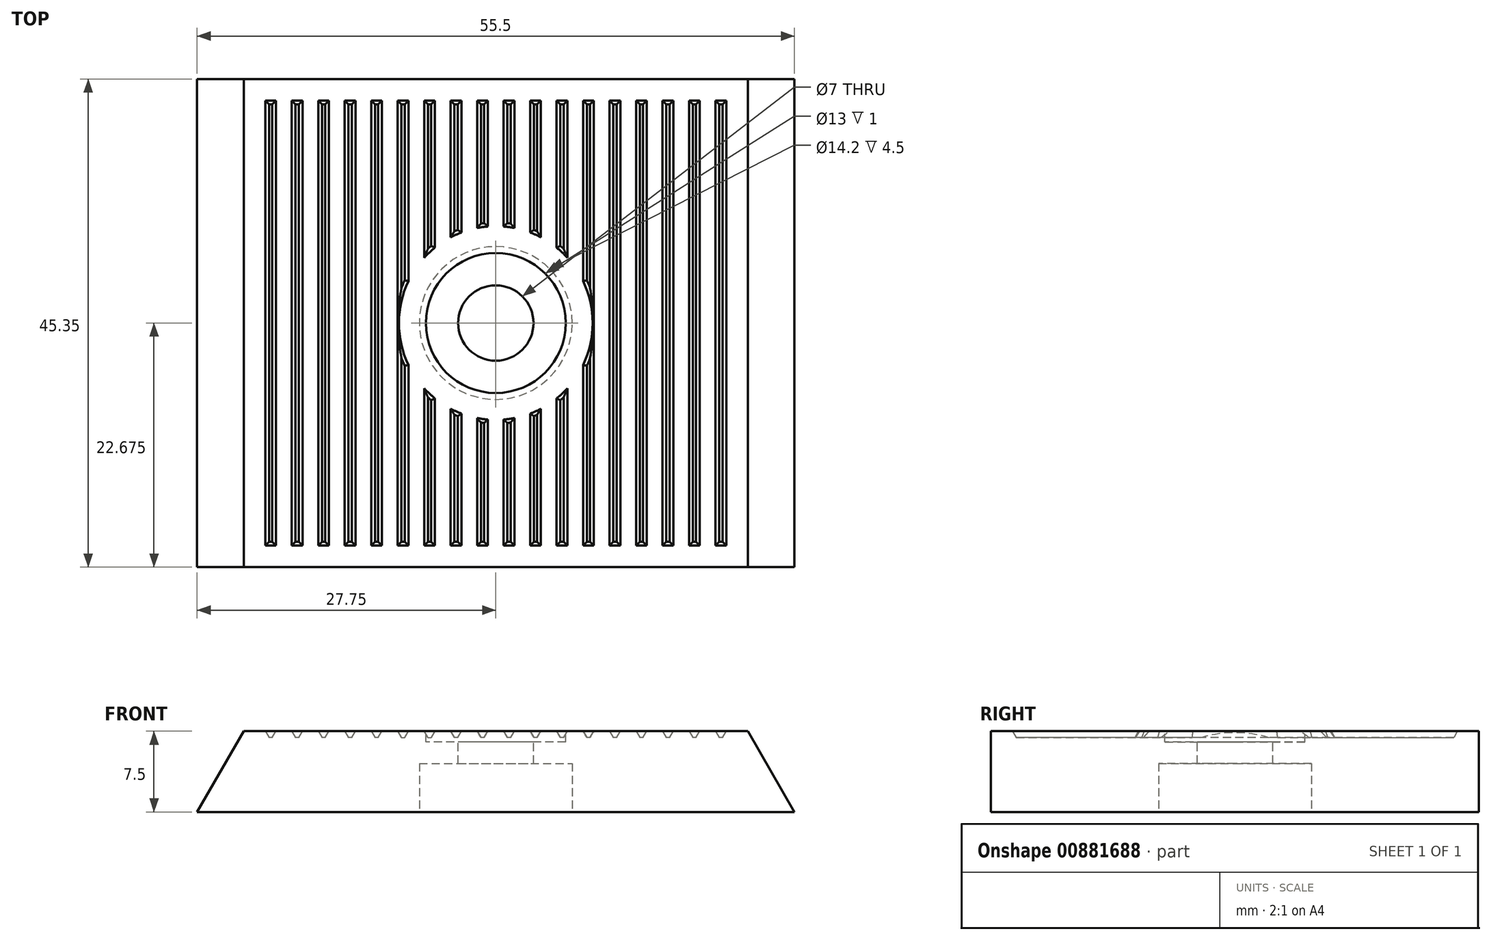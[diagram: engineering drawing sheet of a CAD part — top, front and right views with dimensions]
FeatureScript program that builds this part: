
annotation { "Feature Type Name" : "Feature", "Feature Type Description" : "" }
export const myFeature = defineFeature(function(context is Context, id is Id, definition is map)
    precondition{}
    {
        {
            var Q0;
            Q0=qCreatedBy(makeId("Front.planeOp"),FACE);
            var sketch = newSketch(context, id + "F0", { "sketchPlane" : qUnion([Q0])});
            skLineSegment(sketch, "E0", {"start": v(0, 0) * mm, "end": v(-55.5, 0) * mm});
            skLineSegment(sketch, "E1", {"start": v(-55.5, 0) * mm, "end": v(-51.17, 7.5) * mm});
            skLineSegment(sketch, "E2", {"start": v(-51.17, 7.5) * mm, "end": v(-4.33, 7.5) * mm});
            skLineSegment(sketch, "E3", {"start": v(-4.33, 7.5) * mm, "end": v(0, 0) * mm});
            skSolve(sketch);
        }
        {
            var Q0;
            Q0=makeQuery(id+"F0.imprint","IMPRINT",FACE,{"disambiguationData":[TD([[makeQuery(id+"F0.imprint","IMPRINT",EDGE,{"derivedFrom":sQuery(id+"F0.wireOp",EDGE,"E0")}),-1.0]])]});
            extrude(context, id + "F1", {"entities" : qUnion([Q0]), "depth" : 45.35 * mm, "offsetDistance" : 25 * mm});
        }
        {
            var Q0;
            Q0=makeQuery(id+"F1.opExtrude","SWEPT_FACE",FACE,{"disambiguationData":[OSD([sQuery(id+"F0.wireOp",EDGE,"E2")])]});
            var sketch = newSketch(context, id + "F2", { "sketchPlane" : qUnion([Q0])});
            skLineSegment(sketch, "E4.bottom", {"start": v(-49.17, -2) * mm, "end": v(-48.17, -2) * mm});
            skLineSegment(sketch, "E4.top", {"start": v(-49.17, -43.35) * mm, "end": v(-48.17, -43.35) * mm});
            skLineSegment(sketch, "E4.left", {"start": v(-49.17, -2) * mm, "end": v(-49.17, -43.35) * mm});
            skLineSegment(sketch, "E4.right", {"start": v(-48.17, -2) * mm, "end": v(-48.17, -43.35) * mm});
            skLineSegment(sketch, "E5.1.0.0", {"start": v(-46.7, -2) * mm, "end": v(-46.7, -43.35) * mm});
            skLineSegment(sketch, "E5.1.0.1", {"start": v(-45.7, -2) * mm, "end": v(-45.7, -43.35) * mm});
            skLineSegment(sketch, "E5.1.0.2", {"start": v(-46.7, -2) * mm, "end": v(-45.7, -2) * mm});
            skLineSegment(sketch, "E5.1.0.3", {"start": v(-46.7, -43.35) * mm, "end": v(-45.7, -43.35) * mm});
            skLineSegment(sketch, "E5.2.0.0", {"start": v(-44.25, -2) * mm, "end": v(-44.25, -43.35) * mm});
            skLineSegment(sketch, "E5.2.0.1", {"start": v(-43.25, -2) * mm, "end": v(-43.25, -43.35) * mm});
            skLineSegment(sketch, "E5.2.0.2", {"start": v(-44.25, -2) * mm, "end": v(-43.25, -2) * mm});
            skLineSegment(sketch, "E5.2.0.3", {"start": v(-44.25, -43.35) * mm, "end": v(-43.25, -43.35) * mm});
            skLineSegment(sketch, "E5.direction1", {"start": v(-49.17, -43.35) * mm, "end": v(-46.7, -43.35) * mm, "construction": true});
            skLineSegment(sketch, "E6.0.3.0", {"start": v(-41.79, -2) * mm, "end": v(-41.79, -43.35) * mm});
            skLineSegment(sketch, "E6.3.3.0", {"start": v(-40.79, -2) * mm, "end": v(-40.79, -43.35) * mm});
            skLineSegment(sketch, "E6.6.3.0", {"start": v(-41.79, -2) * mm, "end": v(-40.79, -2) * mm});
            skLineSegment(sketch, "E6.9.3.0", {"start": v(-41.79, -43.35) * mm, "end": v(-40.79, -43.35) * mm});
            skLineSegment(sketch, "E6.0.4.0", {"start": v(-39.33, -2) * mm, "end": v(-39.33, -43.35) * mm});
            skLineSegment(sketch, "E6.3.4.0", {"start": v(-38.33, -2) * mm, "end": v(-38.33, -43.35) * mm});
            skLineSegment(sketch, "E6.6.4.0", {"start": v(-39.33, -2) * mm, "end": v(-38.33, -2) * mm});
            skLineSegment(sketch, "E6.9.4.0", {"start": v(-39.33, -43.35) * mm, "end": v(-38.33, -43.35) * mm});
            skLineSegment(sketch, "E6.0.5.0", {"start": v(-36.86, -2) * mm, "end": v(-36.86, -43.35) * mm});
            skLineSegment(sketch, "E6.3.5.0", {"start": v(-35.86, -2) * mm, "end": v(-35.86, -18.78) * mm});
            skLineSegment(sketch, "E6.6.5.0", {"start": v(-36.86, -2) * mm, "end": v(-35.86, -2) * mm});
            skLineSegment(sketch, "E6.9.5.0", {"start": v(-36.86, -43.35) * mm, "end": v(-35.86, -43.35) * mm});
            skLineSegment(sketch, "E6.0.6.0", {"start": v(-34.4, -2) * mm, "end": v(-34.4, -16.61) * mm});
            skLineSegment(sketch, "E6.3.6.0", {"start": v(-33.4, -2) * mm, "end": v(-33.4, -15.67) * mm});
            skLineSegment(sketch, "E6.6.6.0", {"start": v(-34.4, -2) * mm, "end": v(-33.4, -2) * mm});
            skLineSegment(sketch, "E6.9.6.0", {"start": v(-34.4, -43.35) * mm, "end": v(-33.4, -43.35) * mm});
            skLineSegment(sketch, "E6.0.7.0", {"start": v(-31.94, -2) * mm, "end": v(-31.94, -14.71) * mm});
            skLineSegment(sketch, "E6.3.7.0", {"start": v(-30.94, -2) * mm, "end": v(-30.94, -14.26) * mm});
            skLineSegment(sketch, "E6.6.7.0", {"start": v(-31.94, -2) * mm, "end": v(-30.94, -2) * mm});
            skLineSegment(sketch, "E6.9.7.0", {"start": v(-31.94, -43.35) * mm, "end": v(-30.94, -43.35) * mm});
            skLineSegment(sketch, "E6.0.8.0", {"start": v(-29.48, -2) * mm, "end": v(-29.48, -13.84) * mm});
            skLineSegment(sketch, "E6.3.8.0", {"start": v(-28.48, -2) * mm, "end": v(-28.48, -13.7) * mm});
            skLineSegment(sketch, "E6.6.8.0", {"start": v(-29.48, -2) * mm, "end": v(-28.48, -2) * mm});
            skLineSegment(sketch, "E6.9.8.0", {"start": v(-29.48, -43.35) * mm, "end": v(-28.48, -43.35) * mm});
            skLineSegment(sketch, "E6.0.9.0", {"start": v(-27.02, -2) * mm, "end": v(-27.02, -13.7) * mm});
            skLineSegment(sketch, "E6.3.9.0", {"start": v(-26.02, -2) * mm, "end": v(-26.02, -13.84) * mm});
            skLineSegment(sketch, "E6.6.9.0", {"start": v(-27.02, -2) * mm, "end": v(-26.02, -2) * mm});
            skLineSegment(sketch, "E6.9.9.0", {"start": v(-27.02, -43.35) * mm, "end": v(-26.02, -43.35) * mm});
            skLineSegment(sketch, "E6.0.10.0", {"start": v(-24.56, -2) * mm, "end": v(-24.56, -14.26) * mm});
            skLineSegment(sketch, "E6.3.10.0", {"start": v(-23.56, -2) * mm, "end": v(-23.56, -14.71) * mm});
            skLineSegment(sketch, "E6.6.10.0", {"start": v(-24.56, -2) * mm, "end": v(-23.56, -2) * mm});
            skLineSegment(sketch, "E6.9.10.0", {"start": v(-24.56, -43.35) * mm, "end": v(-23.56, -43.35) * mm});
            skLineSegment(sketch, "E6.0.11.0", {"start": v(-22.1, -2) * mm, "end": v(-22.1, -15.67) * mm});
            skLineSegment(sketch, "E6.3.11.0", {"start": v(-21.1, -2) * mm, "end": v(-21.1, -16.61) * mm});
            skLineSegment(sketch, "E6.6.11.0", {"start": v(-22.1, -2) * mm, "end": v(-21.1, -2) * mm});
            skLineSegment(sketch, "E6.9.11.0", {"start": v(-22.1, -43.35) * mm, "end": v(-21.1, -43.35) * mm});
            skLineSegment(sketch, "E6.0.12.0", {"start": v(-19.64, -2) * mm, "end": v(-19.64, -18.78) * mm});
            skLineSegment(sketch, "E6.3.12.0", {"start": v(-18.64, -2) * mm, "end": v(-18.64, -43.35) * mm});
            skLineSegment(sketch, "E6.6.12.0", {"start": v(-19.64, -2) * mm, "end": v(-18.64, -2) * mm});
            skLineSegment(sketch, "E6.9.12.0", {"start": v(-19.64, -43.35) * mm, "end": v(-18.64, -43.35) * mm});
            skLineSegment(sketch, "E6.0.13.0", {"start": v(-17.17, -2) * mm, "end": v(-17.17, -43.35) * mm});
            skLineSegment(sketch, "E6.3.13.0", {"start": v(-16.17, -2) * mm, "end": v(-16.17, -43.35) * mm});
            skLineSegment(sketch, "E6.6.13.0", {"start": v(-17.17, -2) * mm, "end": v(-16.17, -2) * mm});
            skLineSegment(sketch, "E6.9.13.0", {"start": v(-17.17, -43.35) * mm, "end": v(-16.17, -43.35) * mm});
            skLineSegment(sketch, "E6.0.14.0", {"start": v(-14.71, -2) * mm, "end": v(-14.71, -43.35) * mm});
            skLineSegment(sketch, "E6.3.14.0", {"start": v(-13.71, -2) * mm, "end": v(-13.71, -43.35) * mm});
            skLineSegment(sketch, "E6.6.14.0", {"start": v(-14.71, -2) * mm, "end": v(-13.71, -2) * mm});
            skLineSegment(sketch, "E6.9.14.0", {"start": v(-14.71, -43.35) * mm, "end": v(-13.71, -43.35) * mm});
            skLineSegment(sketch, "E6.0.15.0", {"start": v(-12.25, -2) * mm, "end": v(-12.25, -43.35) * mm});
            skLineSegment(sketch, "E6.3.15.0", {"start": v(-11.25, -2) * mm, "end": v(-11.25, -43.35) * mm});
            skLineSegment(sketch, "E6.6.15.0", {"start": v(-12.25, -2) * mm, "end": v(-11.25, -2) * mm});
            skLineSegment(sketch, "E6.9.15.0", {"start": v(-12.25, -43.35) * mm, "end": v(-11.25, -43.35) * mm});
            skLineSegment(sketch, "E6.0.16.0", {"start": v(-9.8, -2) * mm, "end": v(-9.8, -43.35) * mm});
            skLineSegment(sketch, "E6.3.16.0", {"start": v(-8.8, -2) * mm, "end": v(-8.8, -43.35) * mm});
            skLineSegment(sketch, "E6.6.16.0", {"start": v(-9.8, -2) * mm, "end": v(-8.8, -2) * mm});
            skLineSegment(sketch, "E6.9.16.0", {"start": v(-9.8, -43.35) * mm, "end": v(-8.8, -43.35) * mm});
            skLineSegment(sketch, "E6.0.17.0", {"start": v(-7.33, -2) * mm, "end": v(-7.33, -43.35) * mm});
            skLineSegment(sketch, "E6.3.17.0", {"start": v(-6.33, -2) * mm, "end": v(-6.33, -43.35) * mm});
            skLineSegment(sketch, "E6.6.17.0", {"start": v(-7.33, -2) * mm, "end": v(-6.33, -2) * mm});
            skLineSegment(sketch, "E6.9.17.0", {"start": v(-7.33, -43.35) * mm, "end": v(-6.33, -43.35) * mm});
            skCircle(sketch, "E7.0", {"center": v(-27.75, -22.68) * mm, "radius": 9 * mm});
            skLineSegment(sketch, "E8", {"start": v(-51.17, 0) * mm, "end": v(-4.33, -45.35) * mm, "construction": true});
            skLineSegment(sketch, "E9.trimOffspring", {"start": v(-30.94, -31.1) * mm, "end": v(-30.94, -43.35) * mm});
            skLineSegment(sketch, "E10.trimOffspring", {"start": v(-31.94, -30.64) * mm, "end": v(-31.94, -43.35) * mm});
            skLineSegment(sketch, "E11.trimOffspring", {"start": v(-33.4, -29.68) * mm, "end": v(-33.4, -43.35) * mm});
            skLineSegment(sketch, "E12.trimOffspring", {"start": v(-34.4, -28.74) * mm, "end": v(-34.4, -43.35) * mm});
            skLineSegment(sketch, "E13.trimOffspring", {"start": v(-35.86, -26.57) * mm, "end": v(-35.86, -43.35) * mm});
            skLineSegment(sketch, "E14.trimOffspring", {"start": v(-29.48, -31.5) * mm, "end": v(-29.48, -43.35) * mm});
            skLineSegment(sketch, "E15.trimOffspring", {"start": v(-28.48, -31.65) * mm, "end": v(-28.48, -43.35) * mm});
            skLineSegment(sketch, "E16.trimOffspring", {"start": v(-27.02, -31.65) * mm, "end": v(-27.02, -43.35) * mm});
            skLineSegment(sketch, "E17.trimOffspring", {"start": v(-26.02, -31.5) * mm, "end": v(-26.02, -43.35) * mm});
            skLineSegment(sketch, "E18.trimOffspring", {"start": v(-24.56, -31.1) * mm, "end": v(-24.56, -43.35) * mm});
            skLineSegment(sketch, "E19.trimOffspring", {"start": v(-23.56, -30.64) * mm, "end": v(-23.56, -43.35) * mm});
            skLineSegment(sketch, "E20.trimOffspring", {"start": v(-22.1, -29.68) * mm, "end": v(-22.1, -43.35) * mm});
            skLineSegment(sketch, "E21.trimOffspring", {"start": v(-21.1, -28.74) * mm, "end": v(-21.1, -43.35) * mm});
            skLineSegment(sketch, "E22.trimOffspring", {"start": v(-19.64, -26.57) * mm, "end": v(-19.64, -43.35) * mm});
            skCircle(sketch, "E23", {"center": v(-27.75, -22.68) * mm, "radius": 6.5 * mm});
            skCircle(sketch, "E24", {"center": v(-27.75, -22.68) * mm, "radius": 3.5 * mm});
            skSolve(sketch);
        }
        {
            var Q0;
            Q0=makeQuery(id+"F2.imprint","IMPRINT",FACE,{"disambiguationData":[TD([[makeQuery(id+"F2.imprint","IMPRINT",EDGE,{"derivedFrom":sQuery(id+"F2.wireOp",EDGE,"E4.bottom")}),-1.0]])]});
            var Q1;
            Q1=makeQuery(id+"F2.imprint","IMPRINT",FACE,{"disambiguationData":[TD([[makeQuery(id+"F2.imprint","IMPRINT",EDGE,{"derivedFrom":sQuery(id+"F2.wireOp",EDGE,"E5.1.0.0")}),1.0]])]});
            var Q2;
            Q2=makeQuery(id+"F2.imprint","IMPRINT",FACE,{"disambiguationData":[TD([[makeQuery(id+"F2.imprint","IMPRINT",EDGE,{"derivedFrom":sQuery(id+"F2.wireOp",EDGE,"E5.2.0.0")}),1.0]])]});
            var Q3;
            Q3=makeQuery(id+"F2.imprint","IMPRINT",FACE,{"disambiguationData":[TD([[makeQuery(id+"F2.imprint","IMPRINT",EDGE,{"derivedFrom":sQuery(id+"F2.wireOp",EDGE,"E6.0.3.0")}),1.0]])]});
            var Q4;
            Q4=makeQuery(id+"F2.imprint","IMPRINT",FACE,{"disambiguationData":[TD([[makeQuery(id+"F2.imprint","IMPRINT",EDGE,{"derivedFrom":sQuery(id+"F2.wireOp",EDGE,"E6.0.4.0")}),1.0]])]});
            var Q5;
            Q5=makeQuery(id+"F2.imprint","IMPRINT",FACE,{"disambiguationData":[TD([[makeQuery(id+"F2.imprint","IMPRINT",EDGE,{"derivedFrom":sQuery(id+"F2.wireOp",EDGE,"E6.0.13.0")}),1.0]])]});
            var Q6;
            Q6=makeQuery(id+"F2.imprint","IMPRINT",FACE,{"disambiguationData":[TD([[makeQuery(id+"F2.imprint","IMPRINT",EDGE,{"derivedFrom":sQuery(id+"F2.wireOp",EDGE,"E6.0.14.0")}),1.0]])]});
            var Q7;
            Q7=makeQuery(id+"F2.imprint","IMPRINT",FACE,{"disambiguationData":[TD([[makeQuery(id+"F2.imprint","IMPRINT",EDGE,{"derivedFrom":sQuery(id+"F2.wireOp",EDGE,"E6.0.15.0")}),1.0]])]});
            var Q8;
            Q8=makeQuery(id+"F2.imprint","IMPRINT",FACE,{"disambiguationData":[TD([[makeQuery(id+"F2.imprint","IMPRINT",EDGE,{"derivedFrom":sQuery(id+"F2.wireOp",EDGE,"E6.0.16.0")}),1.0]])]});
            var Q9;
            Q9=makeQuery(id+"F2.imprint","IMPRINT",FACE,{"disambiguationData":[TD([[makeQuery(id+"F2.imprint","IMPRINT",EDGE,{"derivedFrom":sQuery(id+"F2.wireOp",EDGE,"E6.0.17.0")}),1.0]])]});
            var Q10;
            Q10=makeQuery(id+"F2.imprint","IMPRINT",FACE,{"disambiguationData":[TD([[makeQuery(id+"F2.imprint","IMPRINT",EDGE,{"derivedFrom":sQuery(id+"F2.wireOp",EDGE,"E6.0.5.0")}),1.0]])]});
            var Q11;
            {var subQ0=sQuery(id+"F2.wireOp",EDGE,"E6.0.6.0");Q11=makeQuery(id+"F2.imprint","IMPRINT",FACE,{"disambiguationData":[TD([[makeQuery(id+"F2.imprint","IMPRINT",EDGE,{"derivedFrom":subQ0}),1.0]])]});}
            var Q12;
            Q12=makeQuery(id+"F2.imprint","IMPRINT",FACE,{"disambiguationData":[TD([[makeQuery(id+"F2.imprint","IMPRINT",EDGE,{"derivedFrom":sQuery(id+"F2.wireOp",EDGE,"E6.9.6.0")}),1.0]])]});
            var Q13;
            {var subQ0=sQuery(id+"F2.wireOp",EDGE,"E6.0.7.0");Q13=makeQuery(id+"F2.imprint","IMPRINT",FACE,{"disambiguationData":[TD([[makeQuery(id+"F2.imprint","IMPRINT",EDGE,{"derivedFrom":subQ0}),1.0]])]});}
            var Q14;
            Q14=makeQuery(id+"F2.imprint","IMPRINT",FACE,{"disambiguationData":[TD([[makeQuery(id+"F2.imprint","IMPRINT",EDGE,{"derivedFrom":sQuery(id+"F2.wireOp",EDGE,"E6.9.7.0")}),1.0]])]});
            var Q15;
            {var subQ0=sQuery(id+"F2.wireOp",EDGE,"E6.0.8.0");Q15=makeQuery(id+"F2.imprint","IMPRINT",FACE,{"disambiguationData":[TD([[makeQuery(id+"F2.imprint","IMPRINT",EDGE,{"derivedFrom":subQ0}),1.0]])]});}
            var Q16;
            Q16=makeQuery(id+"F2.imprint","IMPRINT",FACE,{"disambiguationData":[TD([[makeQuery(id+"F2.imprint","IMPRINT",EDGE,{"derivedFrom":sQuery(id+"F2.wireOp",EDGE,"E6.9.8.0")}),1.0]])]});
            var Q17;
            {var subQ0=sQuery(id+"F2.wireOp",EDGE,"E6.0.9.0");Q17=makeQuery(id+"F2.imprint","IMPRINT",FACE,{"disambiguationData":[TD([[makeQuery(id+"F2.imprint","IMPRINT",EDGE,{"derivedFrom":subQ0}),1.0]])]});}
            var Q18;
            Q18=makeQuery(id+"F2.imprint","IMPRINT",FACE,{"disambiguationData":[TD([[makeQuery(id+"F2.imprint","IMPRINT",EDGE,{"derivedFrom":sQuery(id+"F2.wireOp",EDGE,"E6.9.9.0")}),1.0]])]});
            var Q19;
            {var subQ0=sQuery(id+"F2.wireOp",EDGE,"E6.0.10.0");Q19=makeQuery(id+"F2.imprint","IMPRINT",FACE,{"disambiguationData":[TD([[makeQuery(id+"F2.imprint","IMPRINT",EDGE,{"derivedFrom":subQ0}),1.0]])]});}
            var Q20;
            Q20=makeQuery(id+"F2.imprint","IMPRINT",FACE,{"disambiguationData":[TD([[makeQuery(id+"F2.imprint","IMPRINT",EDGE,{"derivedFrom":sQuery(id+"F2.wireOp",EDGE,"E6.9.10.0")}),1.0]])]});
            var Q21;
            {var subQ0=sQuery(id+"F2.wireOp",EDGE,"E6.0.11.0");Q21=makeQuery(id+"F2.imprint","IMPRINT",FACE,{"disambiguationData":[TD([[makeQuery(id+"F2.imprint","IMPRINT",EDGE,{"derivedFrom":subQ0}),1.0]])]});}
            var Q22;
            Q22=makeQuery(id+"F2.imprint","IMPRINT",FACE,{"disambiguationData":[TD([[makeQuery(id+"F2.imprint","IMPRINT",EDGE,{"derivedFrom":sQuery(id+"F2.wireOp",EDGE,"E6.9.11.0")}),1.0]])]});
            var Q23;
            {var subQ0=sQuery(id+"F2.wireOp",EDGE,"E6.0.12.0");Q23=makeQuery(id+"F2.imprint","IMPRINT",FACE,{"disambiguationData":[TD([[makeQuery(id+"F2.imprint","IMPRINT",EDGE,{"derivedFrom":subQ0}),1.0]])]});}
            extrude(context, id + "F3", {"entities" : qUnion([Q0, Q1, Q2, Q3, Q4, Q5, Q6, Q7, Q8, Q9, Q10, Q11, Q12, Q13, Q14, Q15, Q16, Q17, Q18, Q19, Q20, Q21, Q22, Q23]), "operationType" : NewBodyOperationType.REMOVE, "oppositeDirection" : true, "depth" : 0.6 * mm, "offsetDistance" : 25 * mm, "hasDraft" : true, "draftAngle" : 30 * degree, "draftPullDirection" : true});
        }
        {
            var Q0;
            Q0=makeQuery(id+"F2.imprint","IMPRINT",FACE,{"disambiguationData":[TD([[makeQuery(id+"F2.imprint","IMPRINT",EDGE,{"derivedFrom":sQuery(id+"F2.wireOp",EDGE,"E23")}),1.0]])]});
            extrude(context, id + "F4", {"entities" : qUnion([Q0]), "operationType" : NewBodyOperationType.REMOVE, "oppositeDirection" : true, "depth" : 1 * mm, "offsetDistance" : 25 * mm});
        }
        {
            var Q0;
            Q0=makeQuery(id+"F2.imprint","IMPRINT",FACE,{"disambiguationData":[TD([[makeQuery(id+"F2.imprint","IMPRINT",EDGE,{"derivedFrom":sQuery(id+"F2.wireOp",EDGE,"E24")}),1.0]])]});
            extrude(context, id + "F5", {"entities" : qUnion([Q0]), "operationType" : NewBodyOperationType.REMOVE, "endBound" : BoundingType.UP_TO_NEXT, "oppositeDirection" : true, "depth" : 25 * mm, "offsetDistance" : 25 * mm});
        }
        {
            var Q0;
            Q0=makeQuery(id+"F1.opExtrude","SWEPT_FACE",FACE,{"disambiguationData":[OSD([sQuery(id+"F0.wireOp",EDGE,"E0")])]});
            var sketch = newSketch(context, id + "F6", { "sketchPlane" : qUnion([Q0])});
            skCircle(sketch, "E25", {"center": v(-27.75, 22.68) * mm, "radius": 7.1 * mm});
            skSolve(sketch);
        }
        {
            var Q0;
            Q0 = qSketchRegion(id + "F6", true);
            extrude(context, id + "F7", {"entities" : qUnion([Q0]), "operationType" : NewBodyOperationType.REMOVE, "oppositeDirection" : true, "depth" : 4.5 * mm, "offsetDistance" : 25 * mm});
        }
    });
